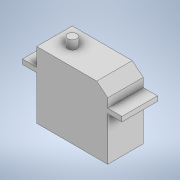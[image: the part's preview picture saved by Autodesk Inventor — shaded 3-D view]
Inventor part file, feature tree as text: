
AUTODESK INVENTOR PART (.ipt)
format: ipt  version: 2020 (Build 240168000, 168)  size: 124,416 bytes
history: native  units: mm
features: extrude x2, sketch x2
ambient origin geometry x8: Origin, YZ Plane, XZ Plane, XY Plane, X Axis, Y Axis, Z Axis, Center Point
bodies: Solid1 (feature_tree)
feature tree (4):
  extrude  "Extrusion1"  Depth=24.7mm
  extrude  "Extrusion3"  Depth=20.0mm TaperAngle=0.0deg
  sketch  "Sketch1"  dims[d0=40.0mm d1=24.7mm]
  sketch  "Sketch3"  dims[d2=2.7mm d3=20.0mm d4=0.0mm d9=37.5mm d13=8.0mm d14=8.0mm d15=8.0mm d16=5.0mm d17=5.0mm d18=10.0mm d19=10.0mm d20=5.0mm d21=0.0mm]
